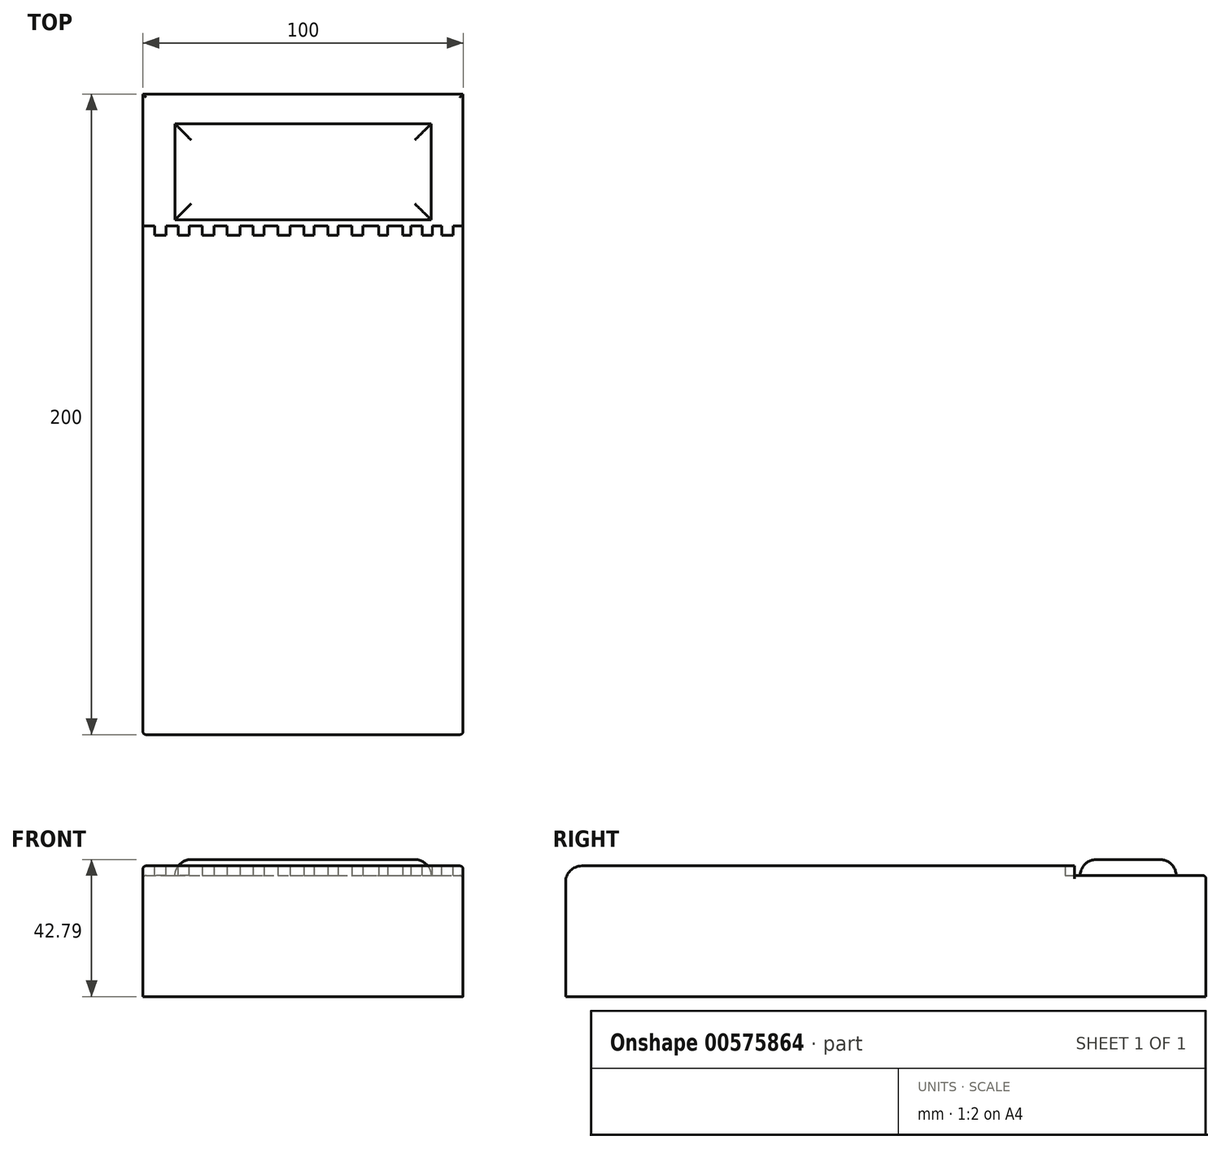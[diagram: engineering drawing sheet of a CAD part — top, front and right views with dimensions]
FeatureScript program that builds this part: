
annotation { "Feature Type Name" : "Feature", "Feature Type Description" : "" }
export const myFeature = defineFeature(function(context is Context, id is Id, definition is map)
    precondition{}
    {
        {
            var Q0;
            Q0=qCreatedBy(makeId("Front.planeOp"),FACE);
            var sketch = newSketch(context, id + "F0", { "sketchPlane" : qUnion([Q0])});
            skLineSegment(sketch, "E0.bottom", {"start": v(-50.31, 41.06) * mm, "end": v(49.69, 41.06) * mm});
            skLineSegment(sketch, "E0.top", {"start": v(-50.31, 3.27) * mm, "end": v(49.69, 3.27) * mm});
            skLineSegment(sketch, "E0.left", {"start": v(-50.31, 41.06) * mm, "end": v(-50.31, 3.27) * mm});
            skLineSegment(sketch, "E0.right", {"start": v(49.69, 41.06) * mm, "end": v(49.69, 3.27) * mm});
            skSolve(sketch);
        }
        {
            var Q0;
            Q0=makeQuery(id+"F0.imprint","IMPRINT",FACE,{"disambiguationData":[TD([[makeQuery(id+"F0.imprint","IMPRINT",EDGE,{"derivedFrom":sQuery(id+"F0.wireOp",EDGE,"E0.bottom")}),-1.0]])]});
            extrude(context, id + "F1", {"entities" : qUnion([Q0]), "depth" : 200 * mm, "offsetDistance" : 25.4 * mm});
        }
        {
            var Q0;
            Q0=makeQuery(id+"F1.opExtrude","SWEPT_FACE",FACE,{"disambiguationData":[OSD([sQuery(id+"F0.wireOp",EDGE,"E0.bottom")])]});
            var sketch = newSketch(context, id + "F2", { "sketchPlane" : qUnion([Q0])});
            skLineSegment(sketch, "E1.bottom", {"start": v(-40.31, -39.3) * mm, "end": v(39.69, -39.3) * mm});
            skLineSegment(sketch, "E1.top", {"start": v(-40.31, -9.3) * mm, "end": v(39.69, -9.3) * mm});
            skLineSegment(sketch, "E1.left", {"start": v(-40.31, -39.3) * mm, "end": v(-40.31, -9.3) * mm});
            skLineSegment(sketch, "E1.right", {"start": v(39.69, -39.3) * mm, "end": v(39.69, -9.3) * mm});
            skSolve(sketch);
        }
        {
            var Q0;
            Q0 = qSketchRegion(id + "F2", true);
            extrude(context, id + "F3", {"entities" : qUnion([Q0]), "operationType" : NewBodyOperationType.ADD, "depth" : 5 * mm, "offsetDistance" : 25.4 * mm});
        }
        {
            var Q0;
            Q0=makeQuery(id+"F3.opExtrude","CAP_EDGE",EDGE,{"disambiguationData":[OSD([sQuery(id+"F2.wireOp",EDGE,"E1.right")])],"isStart":false});
            var Q1;
            Q1=makeQuery(id+"F3.opExtrude","CAP_EDGE",EDGE,{"disambiguationData":[OSD([sQuery(id+"F2.wireOp",EDGE,"E1.top")])],"isStart":false});
            var Q2;
            Q2=makeQuery(id+"F3.opExtrude","CAP_EDGE",EDGE,{"disambiguationData":[OSD([sQuery(id+"F2.wireOp",EDGE,"E1.left")])],"isStart":false});
            var Q3;
            Q3=makeQuery(id+"F3.opExtrude","CAP_EDGE",EDGE,{"disambiguationData":[OSD([sQuery(id+"F2.wireOp",EDGE,"E1.bottom")])],"isStart":false});
            fillet(context, id + "F4", {"entities" : qUnion([Q0, Q1, Q2, Q3]), "radius" : 5.08 * mm, "tangentPropagation" : true, "allowEdgeOverflow" : false});
        }
        {
            var Q0;
            Q0=makeQuery(id+"F1.opExtrude","SWEPT_FACE",FACE,{"disambiguationData":[OSD([sQuery(id+"F0.wireOp",EDGE,"E0.bottom")])]});
            var sketch = newSketch(context, id + "F5", { "sketchPlane" : qUnion([Q0])});
            skLineSegment(sketch, "E2.bottom", {"start": v(-50.31, -200) * mm, "end": v(49.69, -200) * mm});
            skLineSegment(sketch, "E2.top", {"start": v(-50.31, -44.04) * mm, "end": v(49.69, -44.04) * mm});
            skLineSegment(sketch, "E2.left", {"start": v(-50.31, -200) * mm, "end": v(-50.31, -44.04) * mm});
            skLineSegment(sketch, "E2.right", {"start": v(49.69, -200) * mm, "end": v(49.69, -44.04) * mm});
            skSolve(sketch);
        }
        {
            var Q0;
            Q0=makeQuery(id+"F5.imprint","IMPRINT",FACE,{"disambiguationData":[TD([[makeQuery(id+"F5.imprint","IMPRINT",EDGE,{"derivedFrom":sQuery(id+"F5.wireOp",EDGE,"E2.bottom")}),1.0]])]});
            extrude(context, id + "F6", {"entities" : qUnion([Q0]), "operationType" : NewBodyOperationType.ADD, "depth" : 3 * mm, "offsetDistance" : 25.4 * mm});
        }
        {
            var Q0;
            Q0=makeQuery(id+"F1.opExtrude","SWEPT_FACE",FACE,{"disambiguationData":[OSD([sQuery(id+"F0.wireOp",EDGE,"E0.bottom")])]});
            var sketch = newSketch(context, id + "F7", { "sketchPlane" : qUnion([Q0])});
            skLineSegment(sketch, "E3.bottom", {"start": v(-50.31, -44.04) * mm, "end": v(-31.8, -44.04) * mm});
            skLineSegment(sketch, "E3.top", {"start": v(-50.31, -41.11) * mm, "end": v(-31.8, -41.11) * mm});
            skLineSegment(sketch, "E3.left", {"start": v(-50.31, -44.04) * mm, "end": v(-50.31, -41.11) * mm});
            skLineSegment(sketch, "E3.right", {"start": v(-31.8, -44.04) * mm, "end": v(-31.8, -41.11) * mm});
            skLineSegment(sketch, "E4.bottom", {"start": v(-28.05, -44.04) * mm, "end": v(-24.01, -44.04) * mm});
            skLineSegment(sketch, "E4.top", {"start": v(-28.05, -41.11) * mm, "end": v(-24.01, -41.11) * mm});
            skLineSegment(sketch, "E4.left", {"start": v(-28.05, -44.04) * mm, "end": v(-28.05, -41.11) * mm});
            skLineSegment(sketch, "E4.right", {"start": v(-24.01, -44.04) * mm, "end": v(-24.01, -41.11) * mm});
            skLineSegment(sketch, "E5.bottom", {"start": v(-19.98, -44.04) * mm, "end": v(-15.94, -44.04) * mm});
            skLineSegment(sketch, "E5.top", {"start": v(-19.98, -41.11) * mm, "end": v(-15.94, -41.11) * mm});
            skLineSegment(sketch, "E5.left", {"start": v(-19.98, -44.04) * mm, "end": v(-19.98, -41.11) * mm});
            skLineSegment(sketch, "E5.right", {"start": v(-15.94, -44.04) * mm, "end": v(-15.94, -41.11) * mm});
            skLineSegment(sketch, "E6.bottom", {"start": v(-12.48, -44.04) * mm, "end": v(-8.16, -44.04) * mm});
            skLineSegment(sketch, "E6.top", {"start": v(-12.48, -41.11) * mm, "end": v(-8.16, -41.11) * mm});
            skLineSegment(sketch, "E6.left", {"start": v(-12.48, -44.04) * mm, "end": v(-12.48, -41.11) * mm});
            skLineSegment(sketch, "E6.right", {"start": v(-8.16, -44.04) * mm, "end": v(-8.16, -41.11) * mm});
            skLineSegment(sketch, "E7.bottom", {"start": v(-4.4, -44.04) * mm, "end": v(0, -44.04) * mm});
            skLineSegment(sketch, "E7.top", {"start": v(-4.4, -41.11) * mm, "end": v(0, -41.11) * mm});
            skLineSegment(sketch, "E7.left", {"start": v(-4.4, -44.04) * mm, "end": v(-4.4, -41.11) * mm});
            skLineSegment(sketch, "E7.right", {"start": v(0, -44.04) * mm, "end": v(0, -41.11) * mm});
            skLineSegment(sketch, "E8.bottom", {"start": v(3.09, -44.04) * mm, "end": v(7.41, -44.04) * mm});
            skLineSegment(sketch, "E8.top", {"start": v(3.09, -41.11) * mm, "end": v(7.41, -41.11) * mm});
            skLineSegment(sketch, "E8.left", {"start": v(3.09, -44.04) * mm, "end": v(3.09, -41.11) * mm});
            skLineSegment(sketch, "E8.right", {"start": v(7.41, -44.04) * mm, "end": v(7.41, -41.11) * mm});
            skLineSegment(sketch, "E9.bottom", {"start": v(10.58, -44.04) * mm, "end": v(14.9, -44.04) * mm});
            skLineSegment(sketch, "E9.top", {"start": v(10.58, -41.11) * mm, "end": v(14.9, -41.11) * mm});
            skLineSegment(sketch, "E9.left", {"start": v(10.58, -44.04) * mm, "end": v(10.58, -41.11) * mm});
            skLineSegment(sketch, "E9.right", {"start": v(14.9, -44.04) * mm, "end": v(14.9, -41.11) * mm});
            skLineSegment(sketch, "E10.bottom", {"start": v(18.37, -44.04) * mm, "end": v(23.27, -44.04) * mm});
            skLineSegment(sketch, "E10.top", {"start": v(18.37, -41.11) * mm, "end": v(23.27, -41.11) * mm});
            skLineSegment(sketch, "E10.left", {"start": v(18.37, -44.04) * mm, "end": v(18.37, -41.11) * mm});
            skLineSegment(sketch, "E10.right", {"start": v(23.27, -44.04) * mm, "end": v(23.27, -41.11) * mm});
            skLineSegment(sketch, "E11.bottom", {"start": v(26.15, -44.04) * mm, "end": v(30.76, -44.04) * mm});
            skLineSegment(sketch, "E11.top", {"start": v(26.15, -41.11) * mm, "end": v(30.76, -41.11) * mm});
            skLineSegment(sketch, "E11.left", {"start": v(26.15, -44.04) * mm, "end": v(26.15, -41.11) * mm});
            skLineSegment(sketch, "E11.right", {"start": v(30.76, -44.04) * mm, "end": v(30.76, -41.11) * mm});
            skLineSegment(sketch, "E12.bottom", {"start": v(33.36, -44.04) * mm, "end": v(49.69, -44.04) * mm});
            skLineSegment(sketch, "E12.top", {"start": v(33.36, -41.11) * mm, "end": v(49.69, -41.11) * mm});
            skLineSegment(sketch, "E12.left", {"start": v(33.36, -44.04) * mm, "end": v(33.36, -41.11) * mm});
            skLineSegment(sketch, "E12.right", {"start": v(49.69, -44.04) * mm, "end": v(49.69, -41.11) * mm});
            skSolve(sketch);
        }
        {
            var Q0;
            Q0 = qSketchRegion(id + "F7", true);
            extrude(context, id + "F8", {"entities" : qUnion([Q0]), "operationType" : NewBodyOperationType.ADD, "depth" : 3 * mm, "offsetDistance" : 25.4 * mm});
        }
        {
            var Q0;
            Q0=makeQuery(id+"F8.boolean.opBoolean","MERGE",FACE,{"derivedFrom":[makeQuery(id+"F6.opExtrude","CAP_FACE",FACE,{"disambiguationData":[OSD([sQuery(id+"F5.wireOp",EDGE,"E2.bottom"),sQuery(id+"F5.wireOp",EDGE,"E2.top"),sQuery(id+"F5.wireOp",EDGE,"E2.left"),sQuery(id+"F5.wireOp",EDGE,"E2.right")])],"isStart":false}),makeQuery(id+"F8.opExtrude","CAP_FACE",FACE,{"disambiguationData":[OSD([sQuery(id+"F7.wireOp",EDGE,"E3.bottom"),sQuery(id+"F7.wireOp",EDGE,"E3.top"),sQuery(id+"F7.wireOp",EDGE,"E3.left"),sQuery(id+"F7.wireOp",EDGE,"E3.right")])],"isStart":false}),makeQuery(id+"F8.opExtrude","CAP_FACE",FACE,{"disambiguationData":[OSD([sQuery(id+"F7.wireOp",EDGE,"E4.bottom"),sQuery(id+"F7.wireOp",EDGE,"E4.top"),sQuery(id+"F7.wireOp",EDGE,"E4.left"),sQuery(id+"F7.wireOp",EDGE,"E4.right")])],"isStart":false}),makeQuery(id+"F8.opExtrude","CAP_FACE",FACE,{"disambiguationData":[OSD([sQuery(id+"F7.wireOp",EDGE,"E5.bottom"),sQuery(id+"F7.wireOp",EDGE,"E5.top"),sQuery(id+"F7.wireOp",EDGE,"E5.left"),sQuery(id+"F7.wireOp",EDGE,"E5.right")])],"isStart":false}),makeQuery(id+"F8.opExtrude","CAP_FACE",FACE,{"disambiguationData":[OSD([sQuery(id+"F7.wireOp",EDGE,"E6.bottom"),sQuery(id+"F7.wireOp",EDGE,"E6.top"),sQuery(id+"F7.wireOp",EDGE,"E6.left"),sQuery(id+"F7.wireOp",EDGE,"E6.right")])],"isStart":false}),makeQuery(id+"F8.opExtrude","CAP_FACE",FACE,{"disambiguationData":[OSD([sQuery(id+"F7.wireOp",EDGE,"E7.bottom"),sQuery(id+"F7.wireOp",EDGE,"E7.top"),sQuery(id+"F7.wireOp",EDGE,"E7.left"),sQuery(id+"F7.wireOp",EDGE,"E7.right")])],"isStart":false}),makeQuery(id+"F8.opExtrude","CAP_FACE",FACE,{"disambiguationData":[OSD([sQuery(id+"F7.wireOp",EDGE,"E8.bottom"),sQuery(id+"F7.wireOp",EDGE,"E8.top"),sQuery(id+"F7.wireOp",EDGE,"E8.left"),sQuery(id+"F7.wireOp",EDGE,"E8.right")])],"isStart":false}),makeQuery(id+"F8.opExtrude","CAP_FACE",FACE,{"disambiguationData":[OSD([sQuery(id+"F7.wireOp",EDGE,"E9.bottom"),sQuery(id+"F7.wireOp",EDGE,"E9.top"),sQuery(id+"F7.wireOp",EDGE,"E9.left"),sQuery(id+"F7.wireOp",EDGE,"E9.right")])],"isStart":false}),makeQuery(id+"F8.opExtrude","CAP_FACE",FACE,{"disambiguationData":[OSD([sQuery(id+"F7.wireOp",EDGE,"E10.bottom"),sQuery(id+"F7.wireOp",EDGE,"E10.top"),sQuery(id+"F7.wireOp",EDGE,"E10.left"),sQuery(id+"F7.wireOp",EDGE,"E10.right")])],"isStart":false}),makeQuery(id+"F8.opExtrude","CAP_FACE",FACE,{"disambiguationData":[OSD([sQuery(id+"F7.wireOp",EDGE,"E11.bottom"),sQuery(id+"F7.wireOp",EDGE,"E11.top"),sQuery(id+"F7.wireOp",EDGE,"E11.left"),sQuery(id+"F7.wireOp",EDGE,"E11.right")])],"isStart":false}),makeQuery(id+"F8.opExtrude","CAP_FACE",FACE,{"disambiguationData":[OSD([sQuery(id+"F7.wireOp",EDGE,"E12.bottom"),sQuery(id+"F7.wireOp",EDGE,"E12.top"),sQuery(id+"F7.wireOp",EDGE,"E12.left"),sQuery(id+"F7.wireOp",EDGE,"E12.right")])],"isStart":false})]});
            var sketch = newSketch(context, id + "F9", { "sketchPlane" : qUnion([Q0])});
            skLineSegment(sketch, "E13.bottom", {"start": v(-35.83, -44.04) * mm, "end": v(-39.28, -44.04) * mm});
            skLineSegment(sketch, "E13.top", {"start": v(-35.83, -41.11) * mm, "end": v(-39.28, -41.11) * mm});
            skLineSegment(sketch, "E13.left", {"start": v(-35.83, -44.04) * mm, "end": v(-35.83, -41.11) * mm});
            skLineSegment(sketch, "E13.right", {"start": v(-39.28, -44.04) * mm, "end": v(-39.28, -41.11) * mm});
            skLineSegment(sketch, "E14.bottom", {"start": v(-43.08, -44.04) * mm, "end": v(-46.65, -44.04) * mm});
            skLineSegment(sketch, "E14.top", {"start": v(-43.08, -41.11) * mm, "end": v(-46.65, -41.11) * mm});
            skLineSegment(sketch, "E14.left", {"start": v(-43.08, -44.04) * mm, "end": v(-43.08, -41.11) * mm});
            skLineSegment(sketch, "E14.right", {"start": v(-46.65, -44.04) * mm, "end": v(-46.65, -41.11) * mm});
            skLineSegment(sketch, "E15.bottom", {"start": v(36.86, -44.04) * mm, "end": v(40.09, -44.04) * mm});
            skLineSegment(sketch, "E15.top", {"start": v(36.86, -41.11) * mm, "end": v(40.09, -41.11) * mm});
            skLineSegment(sketch, "E15.left", {"start": v(36.86, -44.04) * mm, "end": v(36.86, -41.11) * mm});
            skLineSegment(sketch, "E15.right", {"start": v(40.09, -44.04) * mm, "end": v(40.09, -41.11) * mm});
            skLineSegment(sketch, "E16.bottom", {"start": v(43.08, -44.04) * mm, "end": v(46.54, -44.04) * mm});
            skLineSegment(sketch, "E16.top", {"start": v(43.08, -41.11) * mm, "end": v(46.54, -41.11) * mm});
            skLineSegment(sketch, "E16.left", {"start": v(43.08, -44.04) * mm, "end": v(43.08, -41.11) * mm});
            skLineSegment(sketch, "E16.right", {"start": v(46.54, -44.04) * mm, "end": v(46.54, -41.11) * mm});
            skSolve(sketch);
        }
        {
            var Q0;
            Q0 = qSketchRegion(id + "F9", true);
            extrude(context, id + "F10", {"entities" : qUnion([Q0]), "operationType" : NewBodyOperationType.REMOVE, "oppositeDirection" : true, "depth" : 3 * mm, "offsetDistance" : 25.4 * mm});
        }
        {
            var Q0;
            Q0=makeQuery(id+"F6.opExtrude","CAP_EDGE",EDGE,{"disambiguationData":[OSD([sQuery(id+"F5.wireOp",EDGE,"E2.bottom")])],"isStart":false});
            fillet(context, id + "F11", {"entities" : qUnion([Q0]), "radius" : 5.08 * mm, "tangentPropagation" : true, "allowEdgeOverflow" : false});
        }
        {
            var Q0;
            Q0=makeQuery(id+"F1.opExtrude","SWEPT_EDGE",EDGE,{"disambiguationData":[OSD([sQuery(id+"F0.wireOp",EDGE,"E0.bottom"),sQuery(id+"F0.wireOp",EDGE,"E0.right")])]});
            var Q1;
            Q1=makeQuery(id+"F1.opExtrude","CAP_EDGE",EDGE,{"disambiguationData":[OSD([sQuery(id+"F0.wireOp",EDGE,"E0.bottom")])],"isStart":true});
            var Q2;
            Q2=makeQuery(id+"F1.opExtrude","SWEPT_EDGE",EDGE,{"disambiguationData":[OSD([sQuery(id+"F0.wireOp",EDGE,"E0.bottom"),sQuery(id+"F0.wireOp",EDGE,"E0.left")])]});
            var Q3;
            Q3=makeQuery(id+"F8.boolean.opBoolean","MERGE",EDGE,{"derivedFrom":[makeQuery(id+"F6.opExtrude","CAP_EDGE",EDGE,{"disambiguationData":[OSD([sQuery(id+"F5.wireOp",EDGE,"E2.left")])],"isStart":false}),makeQuery(id+"F8.opExtrude","CAP_EDGE",EDGE,{"disambiguationData":[OSD([sQuery(id+"F7.wireOp",EDGE,"E3.left")])],"isStart":false})]});
            var Q4;
            Q4=makeQuery(id+"F8.boolean.opBoolean","MERGE",EDGE,{"derivedFrom":[makeQuery(id+"F6.opExtrude","CAP_EDGE",EDGE,{"disambiguationData":[OSD([sQuery(id+"F5.wireOp",EDGE,"E2.right")])],"isStart":false}),makeQuery(id+"F8.opExtrude","CAP_EDGE",EDGE,{"disambiguationData":[OSD([sQuery(id+"F7.wireOp",EDGE,"E12.right")])],"isStart":false})]});
            fillet(context, id + "F12", {"entities" : qUnion([Q0, Q1, Q2, Q3, Q4]), "radius" : 1 * mm, "tangentPropagation" : true, "allowEdgeOverflow" : false});
        }
    });
